# Revit family: Prises non verrouilllées 480_500 V
name_source: partatom
category: Installations électriques
revit_build: Autodesk Revit 2018 (Build: 20170223_1515(x64)
units: mm (PartAtom-declared; Revit-internal decimal feet)

## family parameters
Conserver l'orientation des annotations = Non
Cote de connecteur circulaire = Utiliser le diamètre
Couper avec des vides une fois chargée = Non
Hôte = Face
Partagée = Non
Point de calcul de pièce = Non
Type d'élément = Normal

## types (6) — shared parameters
Couleur caractéristique = noir
Elévation par défaut = 1000 mm  [stored 3.28084 ft]
Fabricant = Legrand
Famille produit = 0854-P17 TEMPRA PRO
Position de la Terre h = 7
Prise au standard international pour montage encastré ou saillie avec accessoire permet la connexion d'appareils de puissance = Prise au standard international pour montage encastré ou saillie avec accessoire permet la connexion d'appareils de puissance
Standard CEI ou NFC = CEI
Température maximum d'utilisation = 40
Température minimum d'installation = -5
Température minimum d'utilisation = -25
Tension V = 500 V  50/60 Hz  noir
matériau du boitier = plastique
résistance aux chocs IK = 9
type de raccordement = bornes à vis

## per-type parameters (varying)
| type | Description | Intensité A | Nombre de pôles | classe de protection IP | entraxe de fixation horizontal mm | entraxe de fixation vertical mm | hauteur mm | installation Encastrée E ou Saillie S | largeur mm | profondeur d'encastrement mm | profondeur mm | sans halogène |
| P17 - 63A - 3P+T - IP67 | LG-555592_Panneau prise 63A 3P+T 500V IP67 | 63 A | 4 |  | 77 mm | 85 mm | 106 mm  [stored 0.347769 ft] | encastré | 106 mm  [stored 0.347769 ft] | 84 mm  [stored 0.275591 ft] | 161 mm  [stored 0.528215 ft] | Non |
| P17 - 32A - 3P+T - IP67 | LG-555492_Panneau de montage prise  32A 3P+T 480/500V IP67 | 32 A | 4 |  | 70 mm | 70 mm | 84 mm  [stored 0.275591 ft] | encastré et saillie | 84 mm  [stored 0.275591 ft] | 42 mm | 92 mm | Non |
| P17 - 16A - 3P+T - IP67 | LG-555392_Panneau de montage prise P17 16A 3P+T 480/500V IP67 | 16 A | 4 | IP44 | 70 mm | 70 mm | 84 mm  [stored 0.275591 ft] | encastré et saillie | 84 mm  [stored 0.275591 ft] | 36 mm | 79 mm | Non |
| P17 - 32A - 3P+T - IP44 | LG-555292_Panneau de montage prise P17  32A 3P+T 480/500V IP44 | 32 A | 4 |  | 70 mm | 70 mm | 84 mm  [stored 0.275591 ft] | encastré et saillie | 84 mm  [stored 0.275591 ft] | 42 mm | 87 mm | Oui |
| P17 - 16A - 4P+T - IP44 | LG-555193_Panneau de montage prise P17 16A 4P+T 480/500V IP44 | 16 A | 5 | IP44 | 70 mm | 70 mm | 84 mm  [stored 0.275591 ft] | encastré et saillie | 84 mm  [stored 0.275591 ft] | 37 mm | 76 mm | Oui |
| P17 - 16A - 3P+T - IP44 | LG-555192_Panneau de montage prise P17  16A 3P+T 480/500V IP44 | 16 A | 4 | IP44 | 70 mm | 70 mm | 84 mm  [stored 0.275591 ft] | encastré et saillie | 84 mm  [stored 0.275591 ft] | 36 mm | 74 mm | Oui |

note: [stored X ft] marks values corroborated as IEEE doubles in the binary element streams (Revit-internal decimal feet)
